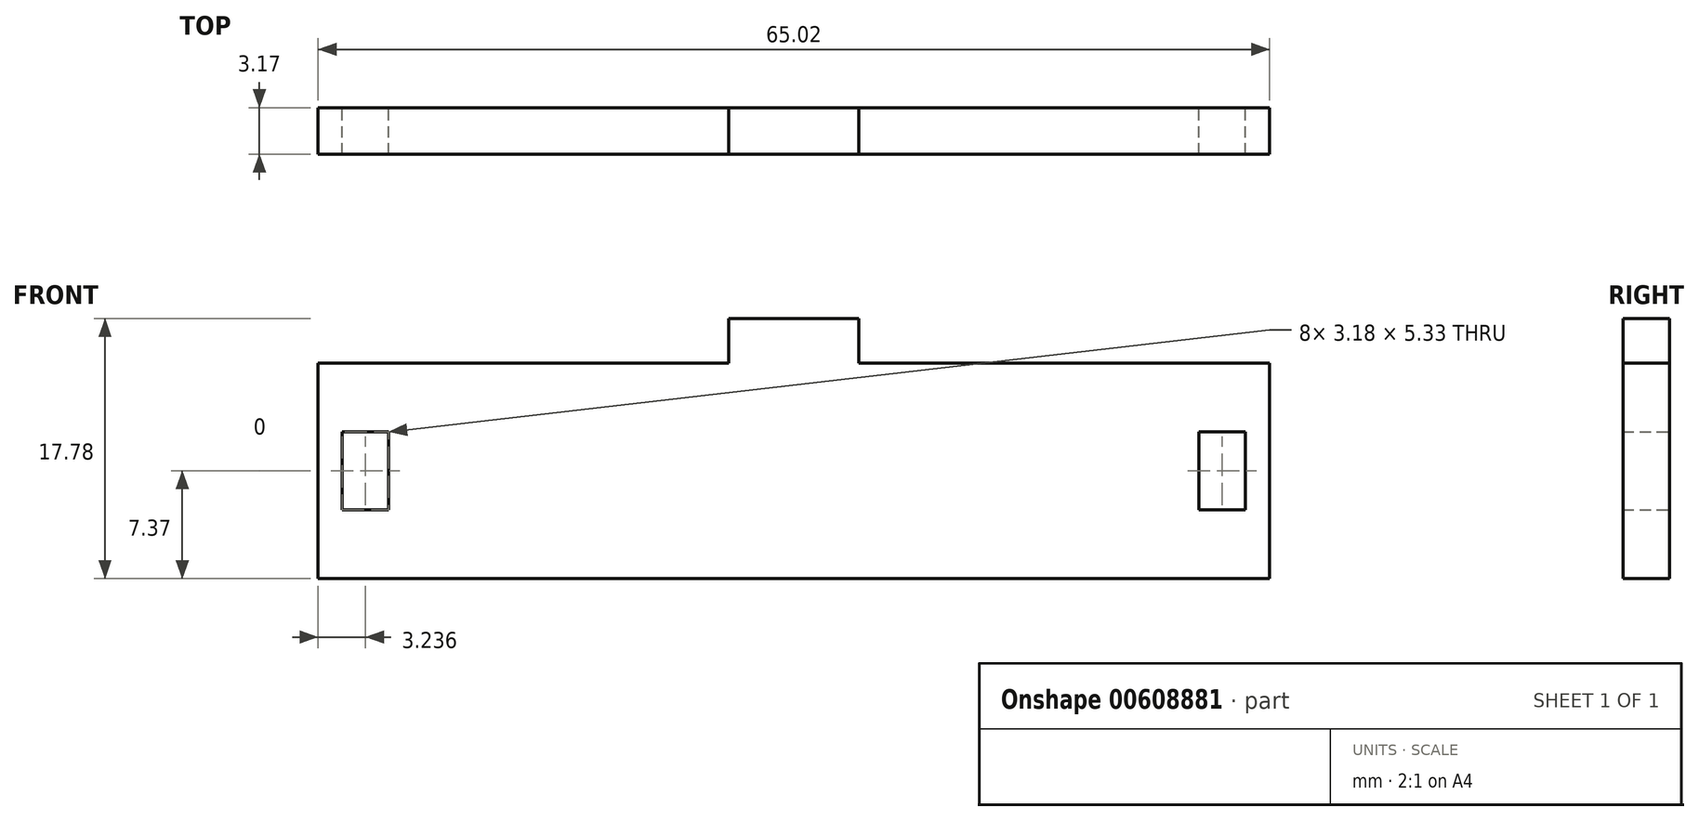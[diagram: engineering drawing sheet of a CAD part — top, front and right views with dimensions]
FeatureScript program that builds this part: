
annotation { "Feature Type Name" : "Feature", "Feature Type Description" : "" }
export const myFeature = defineFeature(function(context is Context, id is Id, definition is map)
    precondition{}
    {
        {
            var Q0;
            Q0=qCreatedBy(makeId("Front.planeOp"),FACE);
            var sketch = newSketch(context, id + "F0", { "sketchPlane" : qUnion([Q0])});
            skLineSegment(sketch, "E0.bottom", {"start": v(-32.51, -7.37) * mm, "end": v(-12.83, -7.37) * mm});
            skLineSegment(sketch, "E0.top", {"start": v(-32.51, 7.37) * mm, "end": v(-4.45, 7.37) * mm});
            skLineSegment(sketch, "E0.left", {"start": v(-32.51, -7.37) * mm, "end": v(-32.51, 7.37) * mm});
            skLineSegment(sketch, "E0.right", {"start": v(32.51, -7.37) * mm, "end": v(32.51, 7.37) * mm});
            skPoint(sketch, "E0.middle", {"position": v(0, 0) * mm});
            skLineSegment(sketch, "E1.0", {"start": v(-4.45, 10.41) * mm, "end": v(4.45, 10.41) * mm});
            skLineSegment(sketch, "E2.0", {"start": v(-4.45, 7.37) * mm, "end": v(-4.45, 10.41) * mm});
            skLineSegment(sketch, "E3.0", {"start": v(4.45, 7.37) * mm, "end": v(4.45, 10.41) * mm});
            skLineSegment(sketch, "E4.trimOffspring", {"start": v(4.45, 7.37) * mm, "end": v(32.51, 7.37) * mm});
            skLineSegment(sketch, "E5.trimOffspring", {"start": v(-12.83, -7.37) * mm, "end": v(18.29, -7.37) * mm});
            skLineSegment(sketch, "E6.trimOffspring", {"start": v(18.29, -7.37) * mm, "end": v(32.51, -7.37) * mm});
            skLineSegment(sketch, "E7.0", {"start": v(-30.86, -2.67) * mm, "end": v(-30.86, 2.67) * mm});
            skLineSegment(sketch, "E8.0", {"start": v(30.86, -2.67) * mm, "end": v(30.86, 2.67) * mm});
            skLineSegment(sketch, "E9.0", {"start": v(27.69, -2.67) * mm, "end": v(27.69, 2.67) * mm});
            skLineSegment(sketch, "E10.0", {"start": v(-27.69, -2.67) * mm, "end": v(-27.69, 2.67) * mm});
            skLineSegment(sketch, "E11.0", {"start": v(-30.86, -2.67) * mm, "end": v(-27.69, -2.67) * mm});
            skLineSegment(sketch, "E12.0", {"start": v(27.69, -2.67) * mm, "end": v(30.86, -2.67) * mm});
            skLineSegment(sketch, "E13.0", {"start": v(27.69, 2.67) * mm, "end": v(30.86, 2.67) * mm});
            skLineSegment(sketch, "E14.0", {"start": v(-30.86, 2.67) * mm, "end": v(-27.69, 2.67) * mm});
            skSolve(sketch);
        }
        {
            var Q0;
            Q0=makeQuery(id+"F0.imprint","IMPRINT",FACE,{"disambiguationData":[TD([[makeQuery(id+"F0.imprint","IMPRINT",EDGE,{"derivedFrom":sQuery(id+"F0.wireOp",EDGE,"E0.bottom")}),1.0]])]});
            extrude(context, id + "F1", {"entities" : qUnion([Q0]), "depth" : 3.17 * mm, "offsetDistance" : 25.4 * mm});
        }
    });
